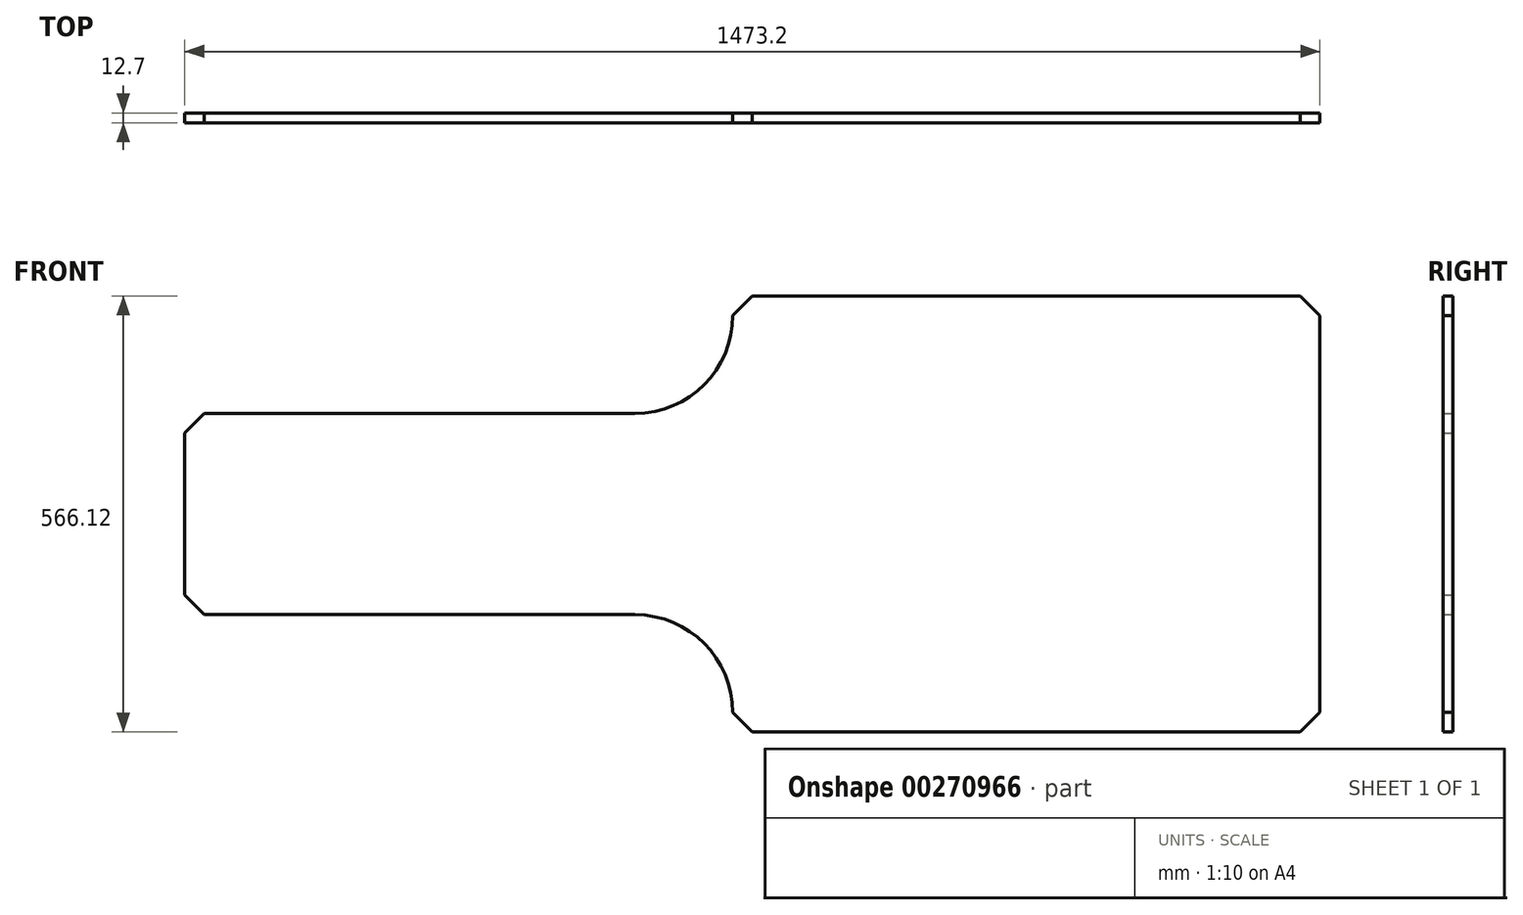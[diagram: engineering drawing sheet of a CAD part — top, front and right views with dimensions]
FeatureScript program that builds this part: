
annotation { "Feature Type Name" : "Feature", "Feature Type Description" : "" }
export const myFeature = defineFeature(function(context is Context, id is Id, definition is map)
    precondition{}
    {
        {
            var Q0;
            Q0=qCreatedBy(makeId("Front.planeOp"),FACE);
            var sketch = newSketch(context, id + "F0", { "sketchPlane" : qUnion([Q0])});
            skLineSegment(sketch, "E0", {"start": v(0, 25.4) * mm, "end": v(0, 540.72) * mm});
            skLineSegment(sketch, "E1", {"start": v(-25.4, 566.12) * mm, "end": v(-736.6, 566.12) * mm});
            skLineSegment(sketch, "E2", {"start": v(-889, 413.72) * mm, "end": v(-1447.8, 413.72) * mm});
            skLineSegment(sketch, "E3", {"start": v(-25.4, 0) * mm, "end": v(-736.6, 0) * mm});
            skLineSegment(sketch, "E4", {"start": v(-889, 152.4) * mm, "end": v(-1447.8, 152.4) * mm});
            skLineSegment(sketch, "E5", {"start": v(-1473.2, 177.8) * mm, "end": v(-1473.2, 388.32) * mm});
            skPoint(sketch, "E6.visualSharp", {"position": v(-762, 413.72) * mm});
            skArc(sketch, "E6.filletArc", {"start": v(-889, 413.72) * mm, "mid": v(-799.2, 450.92) * mm, "end": v(-762, 540.72) * mm});
            skPoint(sketch, "E7.visualSharp", {"position": v(-762, 152.4) * mm});
            skArc(sketch, "E7.filletArc", {"start": v(-762, 25.4) * mm, "mid": v(-799.2, 115.2) * mm, "end": v(-889, 152.4) * mm});
            skLineSegment(sketch, "E8", {"start": v(-736.6, 566.12) * mm, "end": v(-762, 540.72) * mm});
            skLineSegment(sketch, "E9", {"start": v(-736.6, 0) * mm, "end": v(-762, 25.4) * mm});
            skLineSegment(sketch, "E10", {"start": v(-1473.2, 388.32) * mm, "end": v(-1447.8, 413.72) * mm});
            skLineSegment(sketch, "E11", {"start": v(-1473.2, 177.8) * mm, "end": v(-1447.8, 152.4) * mm});
            skLineSegment(sketch, "E12", {"start": v(-25.4, 0) * mm, "end": v(0, 25.4) * mm});
            skLineSegment(sketch, "E13", {"start": v(-25.4, 566.12) * mm, "end": v(0, 540.72) * mm});
            skSolve(sketch);
        }
        {
            var Q0;
            Q0=makeQuery(id+"F0.imprint","IMPRINT",FACE,{"disambiguationData":[TD([[makeQuery(id+"F0.imprint","IMPRINT",EDGE,{"derivedFrom":sQuery(id+"F0.wireOp",EDGE,"E0")}),1.0]])]});
            extrude(context, id + "F1", {"entities" : qUnion([Q0]), "depth" : 12.7 * mm});
        }
    });
